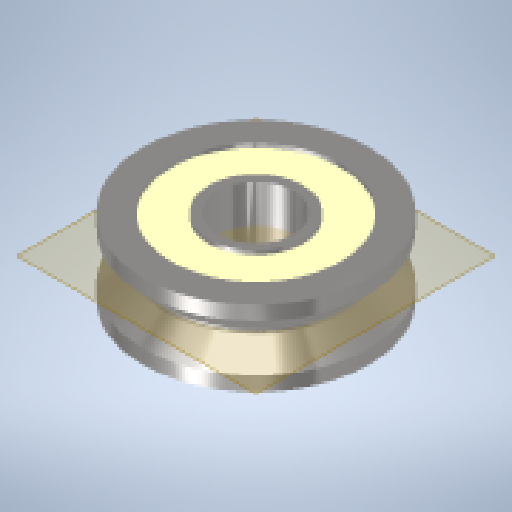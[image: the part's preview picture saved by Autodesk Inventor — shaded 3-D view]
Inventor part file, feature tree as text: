
AUTODESK INVENTOR PART (.ipt)
format: ipt  version: 2024 (Build 280153000, 153)  size: 323,584 bytes
history: native  units: mm
features: extrude x1, plane x1, sketch x1, projected_geometry x1
ambient origin geometry x8: Origin, YZ Plane, XZ Plane, XY Plane, X Axis, Y Axis, Z Axis, Center Point
bodies: Solid1 (feature_tree), Body2 (feature_tree)
feature tree (4):
  extrude  "Extrusion1"  [1 undecoded]
  plane  "Work Plane1"
  sketch  "Sketch1"  dims[d0=0.2mm d1=0.0mm]
  projected_geometry  "Projected Loop1"
note: 1 required parameter value undecoded (feature->parameter linkage not recoverable at this tier; creation-order binding heuristic only, values carry confidence <= 0.55)
